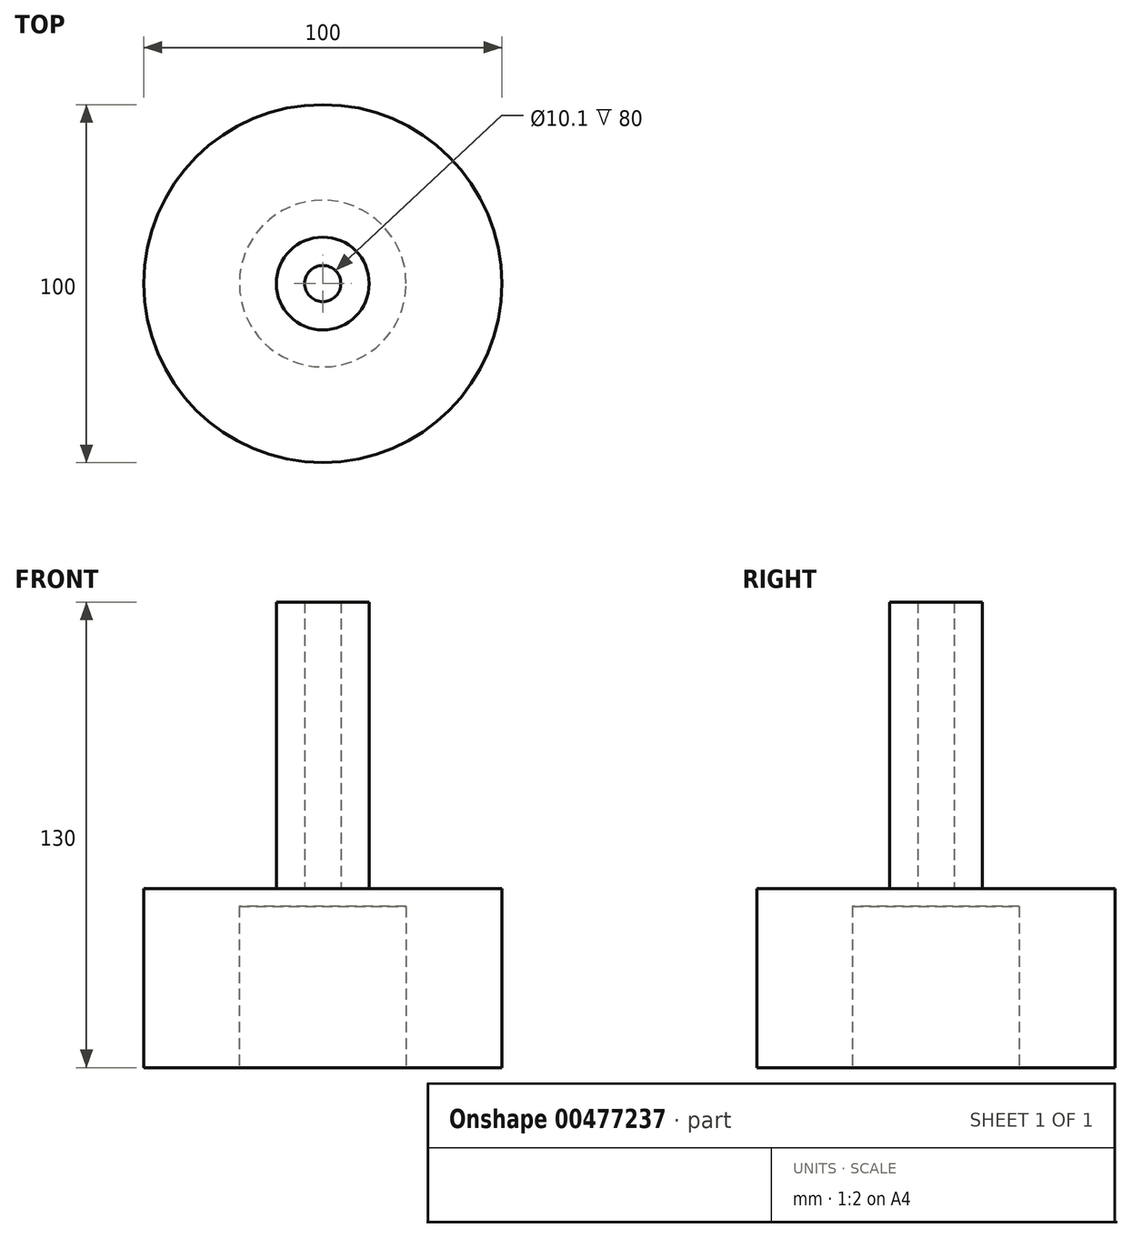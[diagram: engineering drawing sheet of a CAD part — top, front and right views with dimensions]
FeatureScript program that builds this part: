
annotation { "Feature Type Name" : "Feature", "Feature Type Description" : "" }
export const myFeature = defineFeature(function(context is Context, id is Id, definition is map)
    precondition{}
    {
        {
            var Q0;
            Q0=qCreatedBy(makeId("Top.planeOp"),FACE);
            var sketch = newSketch(context, id + "F0", { "sketchPlane" : qUnion([Q0])});
            skCircle(sketch, "E0", {"center": v(-12.4, 3.8) * mm, "radius": 50 * mm});
            skCircle(sketch, "E1", {"center": v(-12.4, 3.8) * mm, "radius": 23.3 * mm});
            skCircle(sketch, "E2", {"center": v(-12.4, 3.8) * mm, "radius": 12.97 * mm});
            skCircle(sketch, "E3", {"center": v(-12.4, 3.8) * mm, "radius": 5.05 * mm});
            skSolve(sketch);
        }
        {
            var Q0;
            Q0 = qSketchRegion(id + "F0", true);
            extrude(context, id + "F1", {"entities" : qUnion([Q0]), "depth" : 50 * mm});
        }
        {
            var Q0;
            Q0=makeQuery(id+"F1.opExtrude","CAP_FACE",FACE,{"disambiguationData":[OSD([sQuery(id+"F0.wireOp",EDGE,"E0"),sQuery(id+"F0.wireOp",EDGE,"E1")])],"isStart":false});
            var sketch = newSketch(context, id + "F2", { "sketchPlane" : qUnion([Q0])});
            skCircle(sketch, "E4.0", {"center": v(-12.4, 3.8) * mm, "radius": 23.3 * mm});
            skSolve(sketch);
        }
        {
            var Q0;
            Q0 = qSketchRegion(id + "F2", true);
            extrude(context, id + "F3", {"entities" : qUnion([Q0]), "operationType" : NewBodyOperationType.ADD, "oppositeDirection" : true, "depth" : 5 * mm});
        }
        {
            var Q0;
            Q0=makeQuery(id+"F3.boolean.opBoolean","MERGE",FACE,{"derivedFrom":[makeQuery(id+"F1.opExtrude","CAP_FACE",FACE,{"disambiguationData":[OSD([sQuery(id+"F0.wireOp",EDGE,"E0"),sQuery(id+"F0.wireOp",EDGE,"E1")])],"isStart":false}),makeQuery(id+"F3.opExtrude","CAP_FACE",FACE,{"disambiguationData":[OSD([sQuery(id+"F2.wireOp",EDGE,"E4.0")])],"isStart":true})]});
            var sketch = newSketch(context, id + "F4", { "sketchPlane" : qUnion([Q0])});
            skCircle(sketch, "E5.0", {"center": v(-12.4, 3.8) * mm, "radius": 12.97 * mm});
            skCircle(sketch, "E6.0", {"center": v(-12.4, 3.8) * mm, "radius": 5.05 * mm});
            skSolve(sketch);
        }
        {
            var Q0;
            Q0 = qSketchRegion(id + "F4", true);
            extrude(context, id + "F5", {"entities" : qUnion([Q0]), "operationType" : NewBodyOperationType.ADD, "depth" : 80 * mm});
        }
    });
